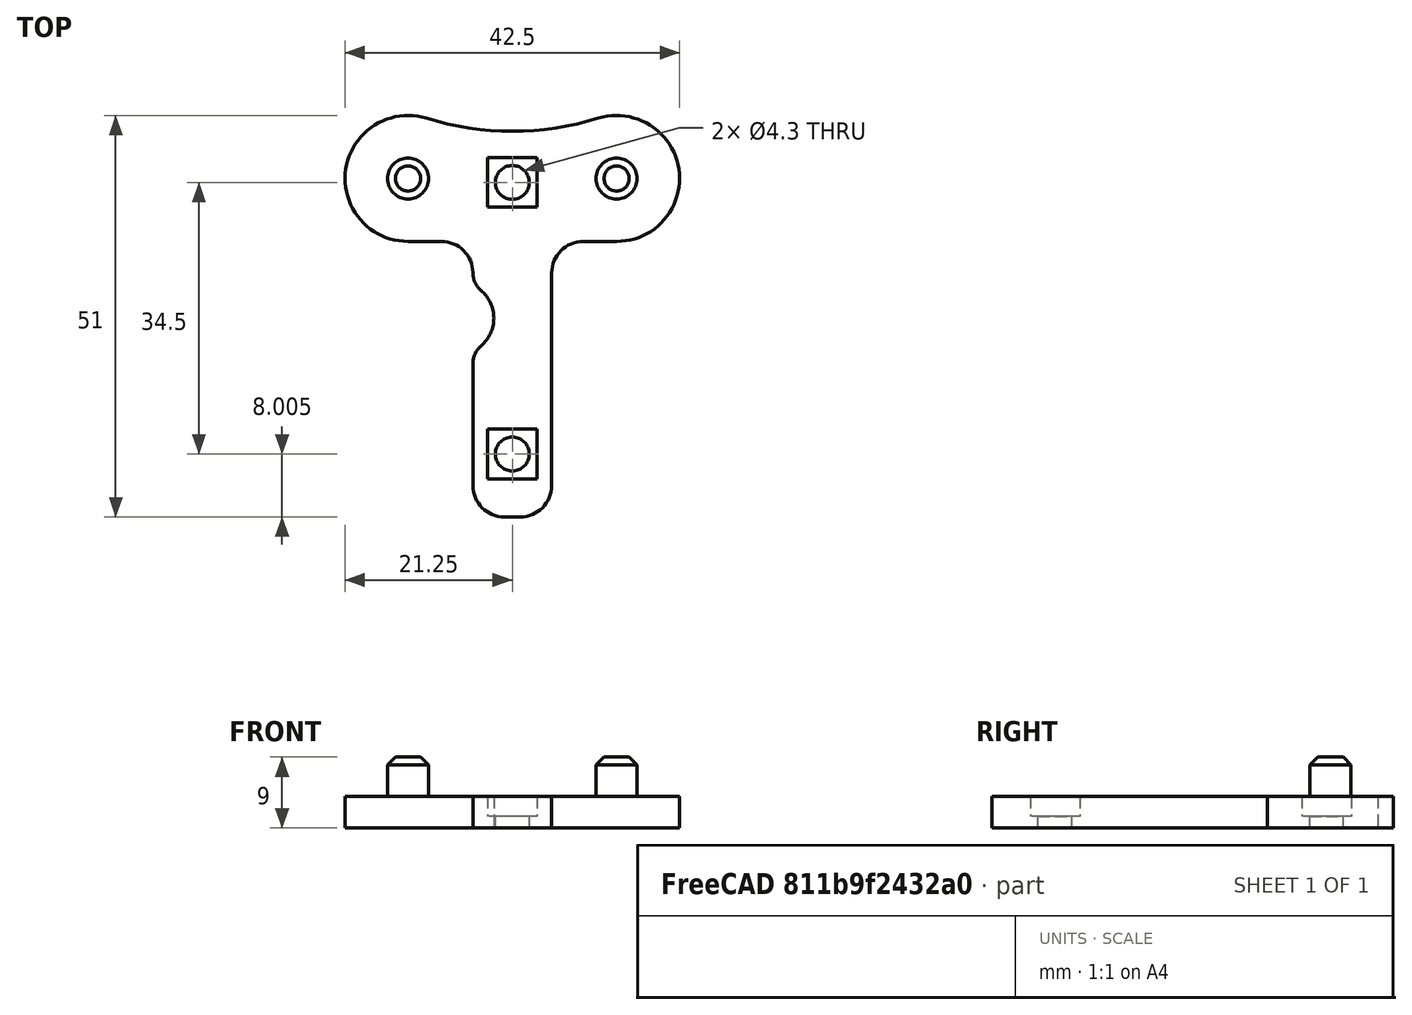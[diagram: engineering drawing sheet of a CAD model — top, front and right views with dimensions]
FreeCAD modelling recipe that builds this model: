
FCSTD DOCUMENT  (FreeCAD 1.0R39109 (Git))
Label: PinceV1
License: All rights reserved
LicenseURL: https://en.wikipedia.org/wiki/All_rights_reserved
objects: Sketcher::SketchObject×5, PartDesign::CoordinateSystem×4, PartDesign::Pocket×3, PartDesign::Pad×2, PartDesign::Fillet×2, PartDesign::Chamfer×1, Mesh::Feature×1, PartDesign::Body×1
note: 39 computed .brp shape members not serialized (recipe doc carries the construction recipe); baked Part::Feature solids carry a one-line shape summary decoded from their .brp

FEATURE [Sketcher::SketchObject] Sketch
  ArcFitTolerance = 0
  AttachmentSupport = -> [XY_Plane]
  FullyConstrained = true
  MakeInternals = false
  MapMode = 5
  sketch-geometry (8):
    g0: ArcOfCircle CenterX=0 CenterY=0 CenterZ=0 NormalX=0 NormalY=0 NormalZ=1 AngleXU=0 Radius=37 StartAngle=4.41351 EndAngle=5.01126
    g1: ArcOfCircle CenterX=-13.25 CenterY=-43.0051 CenterZ=0 NormalX=0 NormalY=0 NormalZ=1 AngleXU=0 Radius=8 StartAngle=1.27192 EndAngle=4.71239
    g2: ArcOfCircle CenterX=13.25 CenterY=-43.0051 CenterZ=0 NormalX=0 NormalY=0 NormalZ=1 AngleXU=0 Radius=8 StartAngle=4.71239 EndAngle=8.15286
    g3: LineSegment StartX=-13.25 StartY=-51.0051 StartZ=0 EndX=-5 EndY=-51.0051 EndZ=0
    g4: LineSegment StartX=13.25 StartY=-51.0051 StartZ=0 EndX=5 EndY=-51.0051 EndZ=0
    g5: LineSegment StartX=-5 StartY=-51.0051 StartZ=0 EndX=-5 EndY=-86.0051 EndZ=0
    g6: LineSegment StartX=5 StartY=-51.0051 StartZ=0 EndX=5 EndY=-86.0051 EndZ=0
    g7: LineSegment StartX=-5 StartY=-86.0051 StartZ=0 EndX=5 EndY=-86.0051 EndZ=0
  constraints (24):
    c: Coincident(g0,g-1)
    c: Radius(g0) = 37
    c: Horizontal(g0,g0)
    c: Radius(g1) = 8
    c: Tangent(g1,g0) = 1.5708
    c: Radius(g2) = 8
    c: Distance(g1,g2) = 26.5
    c: Vertical(g1,g1)
    c: Vertical(g2,g2)
    c: Tangent(g2,g0) = 1.5708
    c: Coincident(g3,g1)
    c: Horizontal(g3)
    c: Coincident(g4,g2)
    c: Horizontal(g4)
    c: Equal(g3,g4)
    c: Distance(g3,g4) = 10
    c: Coincident(g5,g3)
    c: Vertical(g5)
    c: Distance(g5) = 35
    c: Coincident(g6,g4)
    c: Vertical(g6)
    c: Equal(g5,g6)
    c: Coincident(g7,g5)
    c: Coincident(g7,g6)
FEATURE [PartDesign::Pad] Pad
  Direction = (0,0,1)
  Length = 4
  Length2 = 10
  Profile = -> Sketch
  ReferenceAxis = -> Sketch [N_Axis]
  Suppressed = false
  Type = 0
FEATURE [Sketcher::SketchObject] Sketch001
  ArcFitTolerance = 0
  AttachmentSupport = -> [Pad]
  ExternalGeometry = -> [Pad]
  FullyConstrained = true
  MakeInternals = false
  MapMode = 5
  Placement = pos=(0,0,4) rot=(0,0,1;0rad)
  sketch-geometry (2):
    g0: Circle CenterX=-13.25 CenterY=-43.0051 CenterZ=0 NormalX=0 NormalY=0 NormalZ=1 AngleXU=0 Radius=2.6
    g1: Circle CenterX=13.25 CenterY=-43.0051 CenterZ=0 NormalX=0 NormalY=0 NormalZ=1 AngleXU=0 Radius=2.6
  constraints (4):
    c: Coincident(g0,g-3)
    c: Diameter(g0) = 5.2
    c: Coincident(g1,g-4)
    c: Equal(g1,g0)
FEATURE [PartDesign::Pad] Pad001
  BaseFeature = -> Pad
  Direction = (0,0,1)
  Length = 5
  Length2 = 10
  Profile = -> Sketch001
  ReferenceAxis = -> Sketch001 [N_Axis]
  Suppressed = false
  Type = 0
FEATURE [Sketcher::SketchObject] Sketch002
  ArcFitTolerance = 0
  AttachmentSupport = -> [Pad001]
  ExternalGeometry = -> [Pad001]
  FullyConstrained = true
  MakeInternals = false
  MapMode = 5
  Placement = pos=(0,0,4) rot=(0,0,1;0rad)
  sketch-geometry (2):
    g0: Circle CenterX=0 CenterY=-43.5051 CenterZ=0 NormalX=0 NormalY=0 NormalZ=1 AngleXU=0 Radius=2.15
    g1: Circle CenterX=0 CenterY=-78.0051 CenterZ=0 NormalX=0 NormalY=0 NormalZ=1 AngleXU=0 Radius=2.15
  constraints (6):
    c: PointOnObject(g0,g-2)
    c: Diameter(g0) = 4.3
    c: PointOnObject(g1,g-2)
    c: Equal(g0,g1)
    c: Distance(g0,g1) = 34.5
    c: Distance(g0,g-3) = 7.5
FEATURE [PartDesign::Pocket] Pocket
  BaseFeature = -> Pad001
  Direction = (0,0,-1)
  Length = 5
  Length2 = 5
  Profile = -> Sketch002
  ReferenceAxis = -> Sketch002 [N_Axis]
  Suppressed = false
  Type = 1
FEATURE [Sketcher::SketchObject] Sketch003
  ArcFitTolerance = 0
  AttachmentSupport = -> [Pocket]
  ExternalGeometry = -> [Pocket]
  FullyConstrained = true
  MakeInternals = false
  MapMode = 5
  Placement = pos=(0,0,4) rot=(0,0,1;0rad)
  sketch-geometry (10):
    g0: LineSegment StartX=-3.15 StartY=-46.6551 StartZ=0 EndX=-3.15 EndY=-40.3551 EndZ=0
    g1: LineSegment StartX=-3.15 StartY=-40.3551 StartZ=0 EndX=3.15 EndY=-40.3551 EndZ=0
    g2: LineSegment StartX=3.15 StartY=-40.3551 StartZ=0 EndX=3.15 EndY=-46.6551 EndZ=0
    g3: LineSegment StartX=3.15 StartY=-46.6551 StartZ=0 EndX=-3.15 EndY=-46.6551 EndZ=0
    g4: GeomPoint [constr] X=0 Y=-43.5051 Z=0
    g5: LineSegment StartX=-3.15 StartY=-81.1551 StartZ=0 EndX=-3.15 EndY=-74.8551 EndZ=0
    g6: LineSegment StartX=-3.15 StartY=-74.8551 StartZ=0 EndX=3.15 EndY=-74.8551 EndZ=0
    g7: LineSegment StartX=3.15 StartY=-74.8551 StartZ=0 EndX=3.15 EndY=-81.1551 EndZ=0
    g8: LineSegment StartX=3.15 StartY=-81.1551 StartZ=0 EndX=-3.15 EndY=-81.1551 EndZ=0
    g9: GeomPoint [constr] X=0 Y=-78.0051 Z=0
  constraints (24):
    c: Coincident(g0,g1)
    c: Coincident(g1,g2)
    c: Coincident(g2,g3)
    c: Coincident(g3,g0)
    c: Horizontal(g1)
    c: Horizontal(g3)
    c: Vertical(g0)
    c: Vertical(g2)
    c: Symmetric(g1,g0,g4)
    c: Coincident(g4,g-3)
    c: Distance(g1) = 6.3
    c: Equal(g1,g2)
    c: Coincident(g5,g6)
    c: Coincident(g6,g7)
    c: Coincident(g7,g8)
    c: Coincident(g8,g5)
    c: Horizontal(g6)
    c: Horizontal(g8)
    c: Vertical(g5)
    c: Vertical(g7)
    c: Symmetric(g6,g5,g9)
    c: Coincident(g9,g-4)
    c: Equal(g3,g6)
    c: Equal(g6,g7)
FEATURE [PartDesign::Pocket] Pocket001
  BaseFeature = -> Pocket
  Direction = (0,0,-1)
  Length = 2.5
  Length2 = 5
  Profile = -> Sketch003
  ReferenceAxis = -> Sketch003 [N_Axis]
  Suppressed = false
  Type = 0
FEATURE [PartDesign::Fillet] Fillet
  Base = -> Pocket001 [Edge34,Edge33,Edge35,Edge36]
  BaseFeature = -> Pocket001
  Radius = 4
  SupportTransform = false
  Suppressed = false
  UseAllEdges = false
FEATURE [PartDesign::Chamfer] Chamfer
  Angle = 45
  Base = -> Fillet [Edge66,Edge72]
  BaseFeature = -> Fillet
  ChamferType = 0
  FlipDirection = false
  Size = 1
  Size2 = 1
  SupportTransform = false
  Suppressed = false
  UseAllEdges = false
FEATURE [Sketcher::SketchObject] Sketch004
  ArcFitTolerance = 0
  AttachmentSupport = -> [Chamfer]
  ExternalGeometry = -> [Chamfer]
  FullyConstrained = true
  MakeInternals = false
  MapMode = 5
  Placement = pos=(0,0,4) rot=(0,0,1;0rad)
  sketch-geometry (1):
    g0: Circle CenterX=-7 CenterY=-60.7551 CenterZ=0 NormalX=0 NormalY=0 NormalZ=1 AngleXU=0 Radius=4.65
  constraints (3):
    c: Diameter(g0) = 9.3
    c: Distance(g0,g-3) = 2
    c: DistanceY(g0,g-4) = 17.25
FEATURE [PartDesign::Pocket] Pocket002
  BaseFeature = -> Chamfer
  Direction = (0,0,-1)
  Length = 5
  Length2 = 5
  Profile = -> Sketch004
  ReferenceAxis = -> Sketch004 [N_Axis]
  Suppressed = false
  Type = 1
FEATURE [PartDesign::Fillet] Fillet001
  Base = -> Pocket002 [Edge55,Edge52]
  BaseFeature = -> Pocket002
  Radius = 3
  SupportTransform = false
  Suppressed = false
  UseAllEdges = false
FEATURE [Mesh::Feature] Mesh  label="Corps (Meshed)"
FEATURE [PartDesign::CoordinateSystem] LCS_1
  AttacherType = Attacher::AttachEngine3D
  AttachmentSupport = -> [Fillet001]
  MapMode = 11
  Placement = pos=(0,-43.5051,1.5) rot=(0,0,1;1.5708rad)
FEATURE [PartDesign::CoordinateSystem] LCS_2
  AttacherType = Attacher::AttachEngine3D
  AttachmentSupport = -> [Fillet001]
  MapMode = 11
  Placement = pos=(0,-78.0051,1.5) rot=(0,0,1;1.5708rad)
FEATURE [PartDesign::CoordinateSystem] LCS_3
  AttacherType = Attacher::AttachEngine3D
  AttachmentSupport = -> [Fillet001]
  MapMode = 11
  Placement = pos=(13.25,-43.0051,8) rot=(0,0,1;1.5708rad)
FEATURE [PartDesign::CoordinateSystem] LCS_4
  AttacherType = Attacher::AttachEngine3D
  AttachmentSupport = -> [Fillet001]
  MapMode = 11
  Placement = pos=(-13.25,-43.0051,8) rot=(0,0,1;1.5708rad)
FEATURE [PartDesign::Body] Body  label="partie_fixe"
  AllowCompound = false
  Group = -> [Sketch,Pad,Sketch001,Pad001,Sketch002,Pocket,Sketch003,Pocket001,Fillet,Chamfer,Sketch004,Pocket002,Fillet001,LCS_1,LCS_2,LCS_3,LCS_4]
  Origin = -> Origin
  Tip = -> Fillet001
